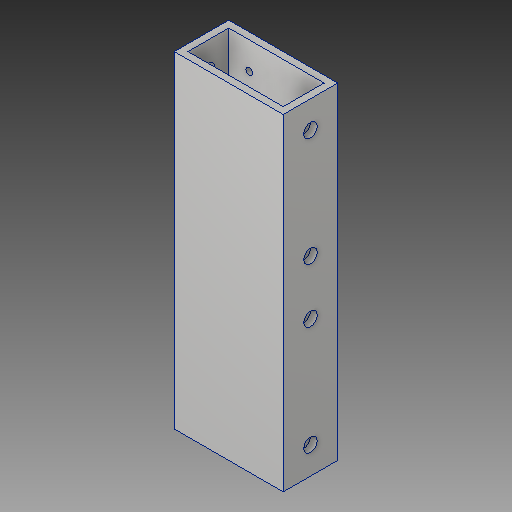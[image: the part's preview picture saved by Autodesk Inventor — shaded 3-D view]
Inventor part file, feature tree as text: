
AUTODESK INVENTOR PART (.ipt)
format: ipt  version: 2017 (Build 210142000, 142)  size: 138,752 bytes
history: native  units: in
note: dims shown in document units (in); Inventor stores cm internally (conversion verified against a paired STEP export)
features: sketch x3, hole x2, extrude x1
ambient origin geometry x8: Origin, YZ Plane, XZ Plane, XY Plane, X Axis, Y Axis, Z Axis, Center Point
bodies: Solid1 (feature_tree)
feature tree (6):
  extrude  "Extrusion1"  Depth=1.0in
  hole  "Hole2"  [1 undecoded]
  hole  "Hole3"  [1 undecoded]
  sketch  "Sketch1"  dims[d0=2.0in d1=1.0in]
  sketch  "Sketch2"  dims[d2=1.75in d3=0.75in]
  sketch  "Sketch3"  dims[d4=0.125in d5=0.125in d6=6.0in d7=0.0in d8=0.25in d9=0.5in d10=0.25in d11=0.5in d19=0.25in d20=0.75in d21=0.375in d22=0.25in d23=0.5635in d24=1.0in d25=0.8108in d27=0.5in d28=0.5in d30=0.125in d31=1.0in d32=0.125in d33=0.75in d34=0.375in d35=0.25in d36=0.5635in d37=0.125in d38=0.8108in]
note: 2 required parameter values undecoded (feature->parameter linkage not recoverable at this tier; creation-order binding heuristic only, values carry confidence <= 0.55)
